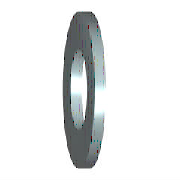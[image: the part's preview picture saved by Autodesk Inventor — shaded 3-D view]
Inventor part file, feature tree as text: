
AUTODESK INVENTOR PART (.ipt)
format: ipt  version: 2016 (Build 200138000, 138)  size: 105,984 bytes
history: native  units: mm (DEFAULTED — no unit token found)
features: other x1, plane x1, sketch x1
ambient origin geometry x7: Origin, YZ Plane, XY Plane, X Axis, Y Axis, Z Axis, Center Point
bodies: Solid1 (feature_tree), Body (feature_tree)
feature tree (3):
  other  "Work Axis1"
  plane  "Work Plane1"
  sketch  "Sketch"  dims[d0=10.5mm d1=20.0mm d2=2.0mm d3=0.0mm d4=0.0mm d5=0.0mm d6=0.0mm d7=0.0mm]
